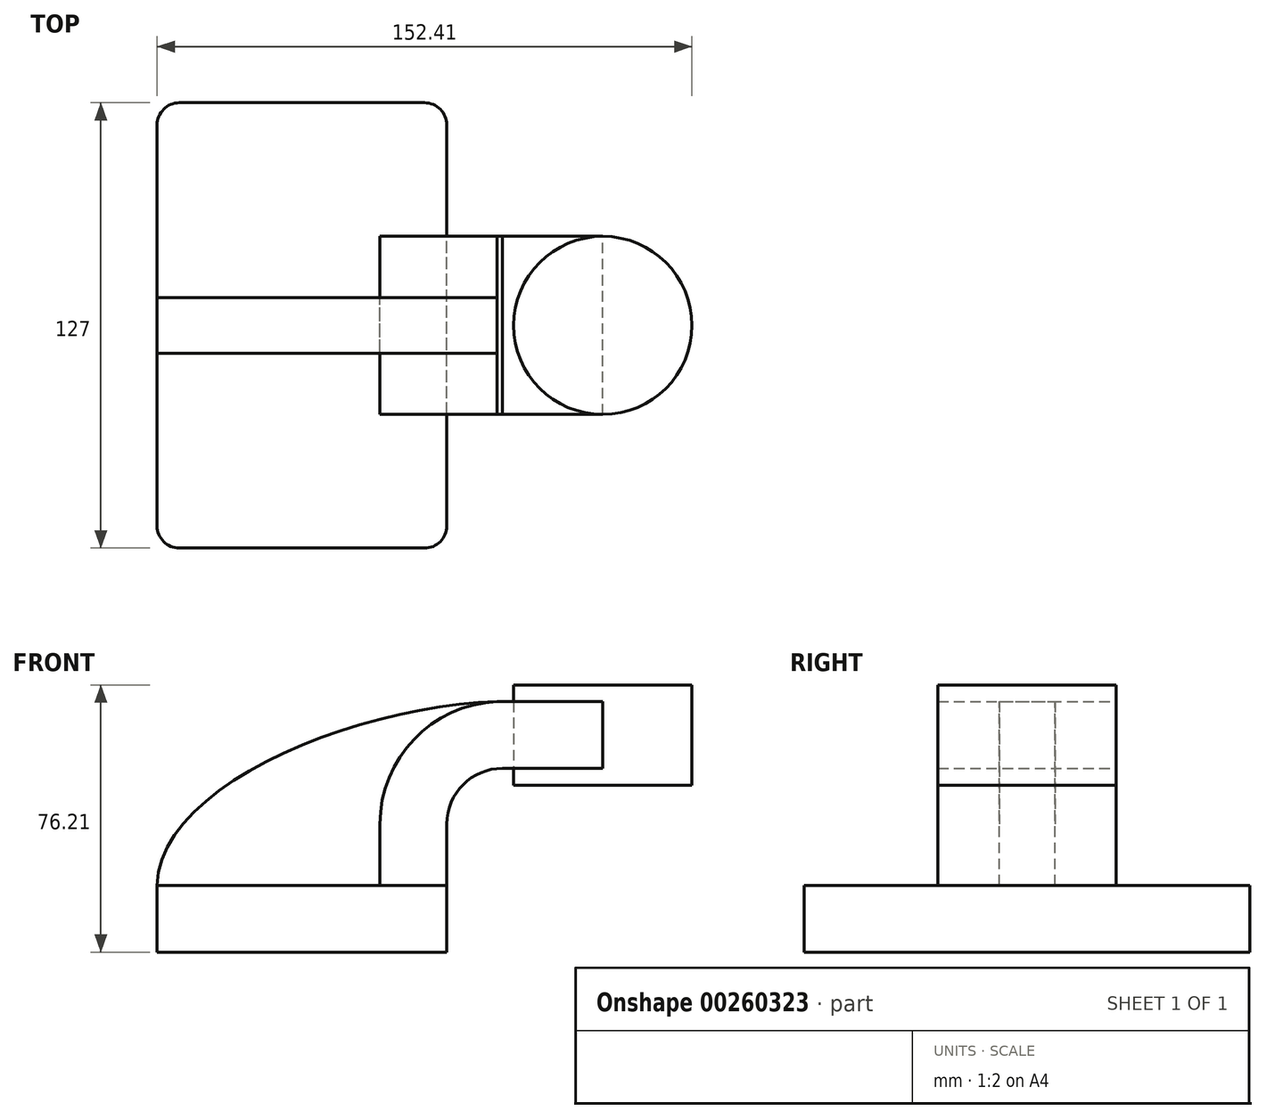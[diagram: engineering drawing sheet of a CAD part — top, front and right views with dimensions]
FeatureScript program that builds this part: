
annotation { "Feature Type Name" : "Feature", "Feature Type Description" : "" }
export const myFeature = defineFeature(function(context is Context, id is Id, definition is map)
    precondition{}
    {
        {
            var Q0;
            Q0=qCreatedBy(makeId("Front.planeOp"),FACE);
            var sketch = newSketch(context, id + "F0", { "sketchPlane" : qUnion([Q0])});
            skLineSegment(sketch, "E0.bottom", {"start": v(-41.28, -9.53) * mm, "end": v(41.28, -9.53) * mm});
            skLineSegment(sketch, "E0.top", {"start": v(-41.28, 9.53) * mm, "end": v(41.28, 9.53) * mm});
            skLineSegment(sketch, "E0.left", {"start": v(-41.28, -9.53) * mm, "end": v(-41.28, 9.53) * mm});
            skLineSegment(sketch, "E0.right", {"start": v(41.28, -9.53) * mm, "end": v(41.28, 9.53) * mm});
            skPoint(sketch, "E0.middle", {"position": v(0, 0) * mm});
            skLineSegment(sketch, "E1.bottom", {"start": v(60.32, 38.1) * mm, "end": v(111.12, 38.1) * mm});
            skLineSegment(sketch, "E1.top", {"start": v(60.32, 66.67) * mm, "end": v(111.12, 66.67) * mm});
            skLineSegment(sketch, "E1.left", {"start": v(60.32, 38.1) * mm, "end": v(60.32, 66.67) * mm});
            skLineSegment(sketch, "E1.right", {"start": v(111.12, 38.1) * mm, "end": v(111.12, 66.67) * mm});
            skPoint(sketch, "E1.middle", {"position": v(85.72, 52.39) * mm});
            skLineSegment(sketch, "E2", {"start": v(41.27, 9.53) * mm, "end": v(41.27, 27) * mm});
            skArc(sketch, "E3", {"start": v(41.27, 27) * mm, "mid": v(45.92, 38.23) * mm, "end": v(57.15, 42.88) * mm});
            skLineSegment(sketch, "E4", {"start": v(57.15, 42.88) * mm, "end": v(85.72, 42.88) * mm});
            skLineSegment(sketch, "E5.0", {"start": v(57.15, 61.93) * mm, "end": v(85.72, 61.93) * mm});
            skArc(sketch, "E5.1", {"start": v(22.23, 27) * mm, "mid": v(32.45, 51.7) * mm, "end": v(57.15, 61.93) * mm});
            skLineSegment(sketch, "E5.2", {"start": v(22.22, 9.53) * mm, "end": v(22.22, 27) * mm});
            skLineSegment(sketch, "E6", {"start": v(85.72, 38.1) * mm, "end": v(85.72, 66.67) * mm});
            skFitSpline(sketch, "E7", {"points": [v(-41.28, 9.53) * mm, v(57.15, 61.93) * mm], "startDerivative": vector(1.38, 86.89) * mm, "endDerivative": vector(121, 1.84) * mm});
            skSolve(sketch);
        }
        {
            var Q0;
            Q0=makeQuery(id+"F0.imprint","IMPRINT",FACE,{"disambiguationData":[TD([[makeQuery(id+"F0.imprint","IMPRINT",EDGE,{"derivedFrom":sQuery(id+"F0.wireOp",EDGE,"E0.bottom")}),1.0]])]});
            extrude(context, id + "F1", {"entities" : qUnion([Q0]), "endBound" : BoundingType.SYMMETRIC, "depth" : 127 * mm});
        }
        {
            var Q0;
            {var subQ1=sQuery(id+"F0.wireOp",EDGE,"E2");Q0=makeQuery(id+"F0.imprint","IMPRINT",FACE,{"disambiguationData":[TD([[makeQuery(id+"F0.imprint","IMPRINT",EDGE,{"derivedFrom":subQ1}),1.0]])]});}
            var Q1;
            {var subQ0=sQuery(id+"F0.wireOp",EDGE,"E4");var subQ1=sQuery(id+"F0.wireOp",EDGE,"E1.left");var subQ2=makeQuery(id+"F0.imprint","INTERSECT",VERTEX,{"derivedFrom":[subQ1,subQ0]});Q1=makeQuery(id+"F0.imprint","IMPRINT",FACE,{"disambiguationData":[TD([[makeQuery(id+"F0.imprint","IMPRINT",EDGE,{"disambiguationData":[TD([[subQ2,-1.0]])],"derivedFrom":subQ1}),-1.0]])]});}
            extrude(context, id + "F2", {"entities" : qUnion([Q0, Q1]), "endBound" : BoundingType.SYMMETRIC, "depth" : 50.8 * mm});
        }
        {
            var Q0;
            {var subQ3=sQuery(id+"F0.wireOp",EDGE,"E5.2");Q0=makeQuery(id+"F0.imprint","IMPRINT",FACE,{"disambiguationData":[TD([[makeQuery(id+"F0.imprint","IMPRINT",EDGE,{"derivedFrom":subQ3}),1.0]])]});}
            extrude(context, id + "F3", {"entities" : qUnion([Q0]), "endBound" : BoundingType.SYMMETRIC, "depth" : 15.88 * mm});
        }
        {
            var Q0;
            {var subQ0=sQuery(id+"F0.wireOp",EDGE,"E1.right");Q0=makeQuery(id+"F0.imprint","IMPRINT",FACE,{"disambiguationData":[TD([[makeQuery(id+"F0.imprint","IMPRINT",EDGE,{"derivedFrom":subQ0}),1.0]])]});}
            var Q1;
            Q1=sQuery(id+"F0.wireOp",EDGE,"E6");
            revolve(context, id + "F4", {"entities" : qUnion([Q0]), "axis" : qUnion([Q1]), "revolveType" : RevolveType.FULL});
        }
        {
            var Q0;
            Q0=makeQuery(id+"F1.opExtrude","CAP_EDGE",EDGE,{"disambiguationData":[OSD([sQuery(id+"F0.wireOp",EDGE,"E0.right")])],"isStart":false});
            var Q1;
            Q1=makeQuery(id+"F1.opExtrude","CAP_EDGE",EDGE,{"disambiguationData":[OSD([sQuery(id+"F0.wireOp",EDGE,"E0.left")])],"isStart":false});
            var Q2;
            Q2=makeQuery(id+"F1.opExtrude","CAP_EDGE",EDGE,{"disambiguationData":[OSD([sQuery(id+"F0.wireOp",EDGE,"E0.left")])],"isStart":true});
            var Q3;
            Q3=makeQuery(id+"F1.opExtrude","CAP_EDGE",EDGE,{"disambiguationData":[OSD([sQuery(id+"F0.wireOp",EDGE,"E0.right")])],"isStart":true});
            fillet(context, id + "F5", {"entities" : qUnion([Q0, Q1, Q2, Q3]), "radius" : 6.35 * mm, "tangentPropagation" : true, "allowEdgeOverflow" : false});
        }
    });
